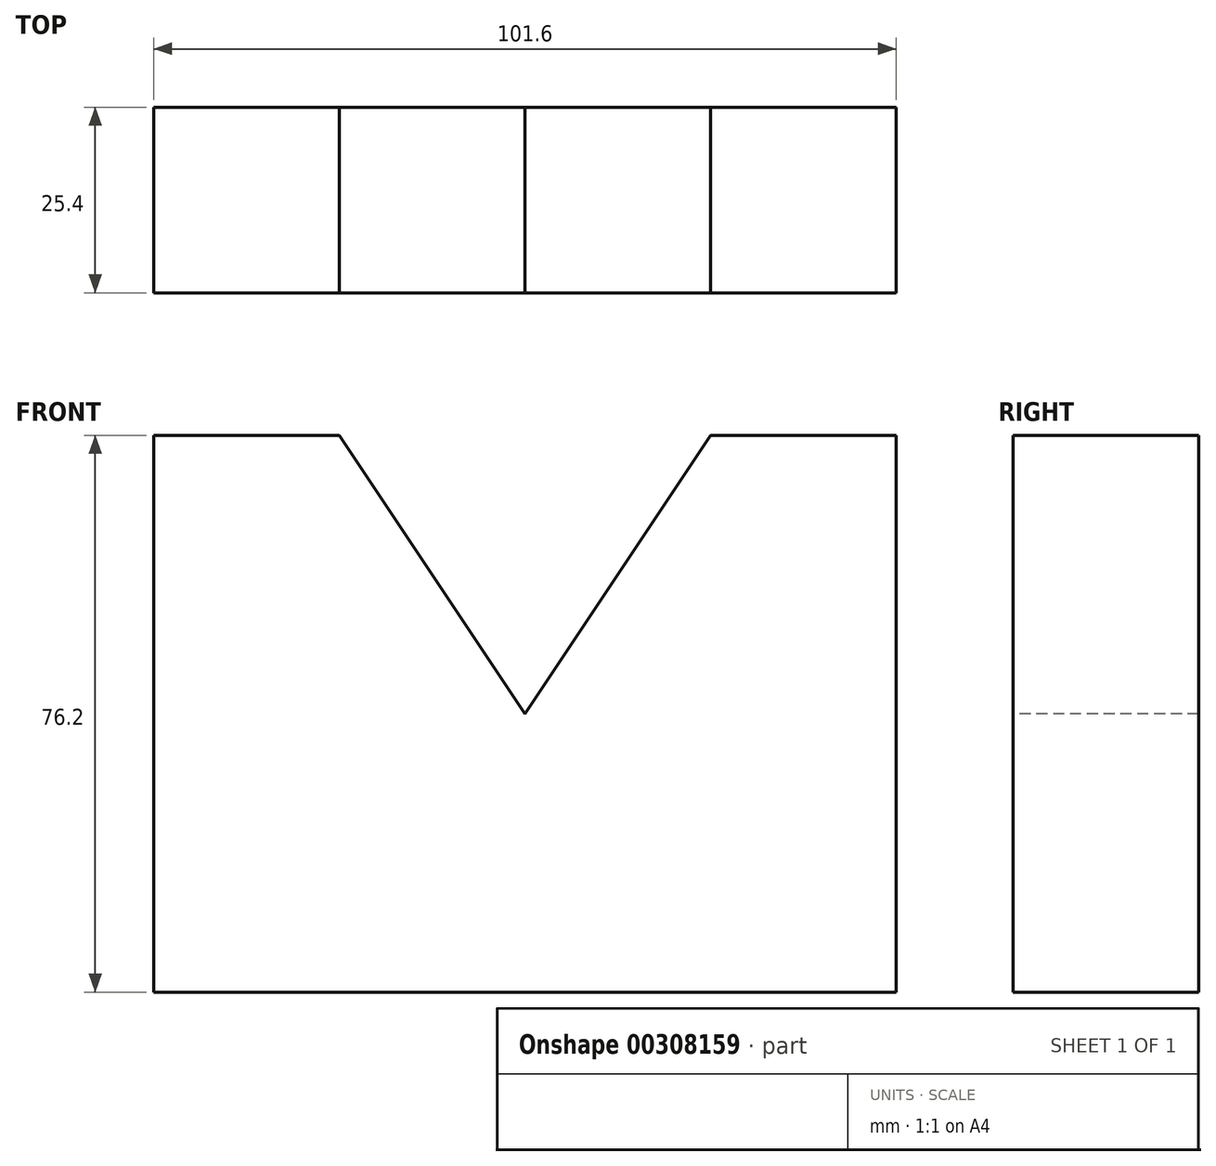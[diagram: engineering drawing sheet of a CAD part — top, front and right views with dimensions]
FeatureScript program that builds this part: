
annotation { "Feature Type Name" : "Feature", "Feature Type Description" : "" }
export const myFeature = defineFeature(function(context is Context, id is Id, definition is map)
    precondition{}
    {
        {
            var Q0;
            Q0=qCreatedBy(makeId("Front.planeOp"),FACE);
            var sketch = newSketch(context, id + "F0", { "sketchPlane" : qUnion([Q0])});
            skLineSegment(sketch, "E0", {"start": v(-59.62, 48.39) * mm, "end": v(-34.22, 48.39) * mm});
            skLineSegment(sketch, "E1", {"start": v(-59.62, 48.39) * mm, "end": v(-59.62, -27.81) * mm});
            skLineSegment(sketch, "E2", {"start": v(-59.62, -27.81) * mm, "end": v(41.98, -27.81) * mm});
            skLineSegment(sketch, "E3", {"start": v(41.98, -27.81) * mm, "end": v(41.98, 48.39) * mm});
            skLineSegment(sketch, "E4", {"start": v(41.98, 48.39) * mm, "end": v(16.58, 48.39) * mm});
            skLineSegment(sketch, "E5", {"start": v(-34.22, 48.39) * mm, "end": v(-8.82, 10.29) * mm});
            skLineSegment(sketch, "E6", {"start": v(16.58, 48.39) * mm, "end": v(-8.82, 10.29) * mm});
            skSolve(sketch);
        }
        {
            var Q0;
            Q0=makeQuery(id+"F0.imprint","IMPRINT",FACE,{"disambiguationData":[TD([[makeQuery(id+"F0.imprint","IMPRINT",EDGE,{"derivedFrom":sQuery(id+"F0.wireOp",EDGE,"E0")}),-1.0]])]});
            extrude(context, id + "F1", {"entities" : qUnion([Q0]), "oppositeDirection" : true, "depth" : 25.4 * mm});
        }
    });
